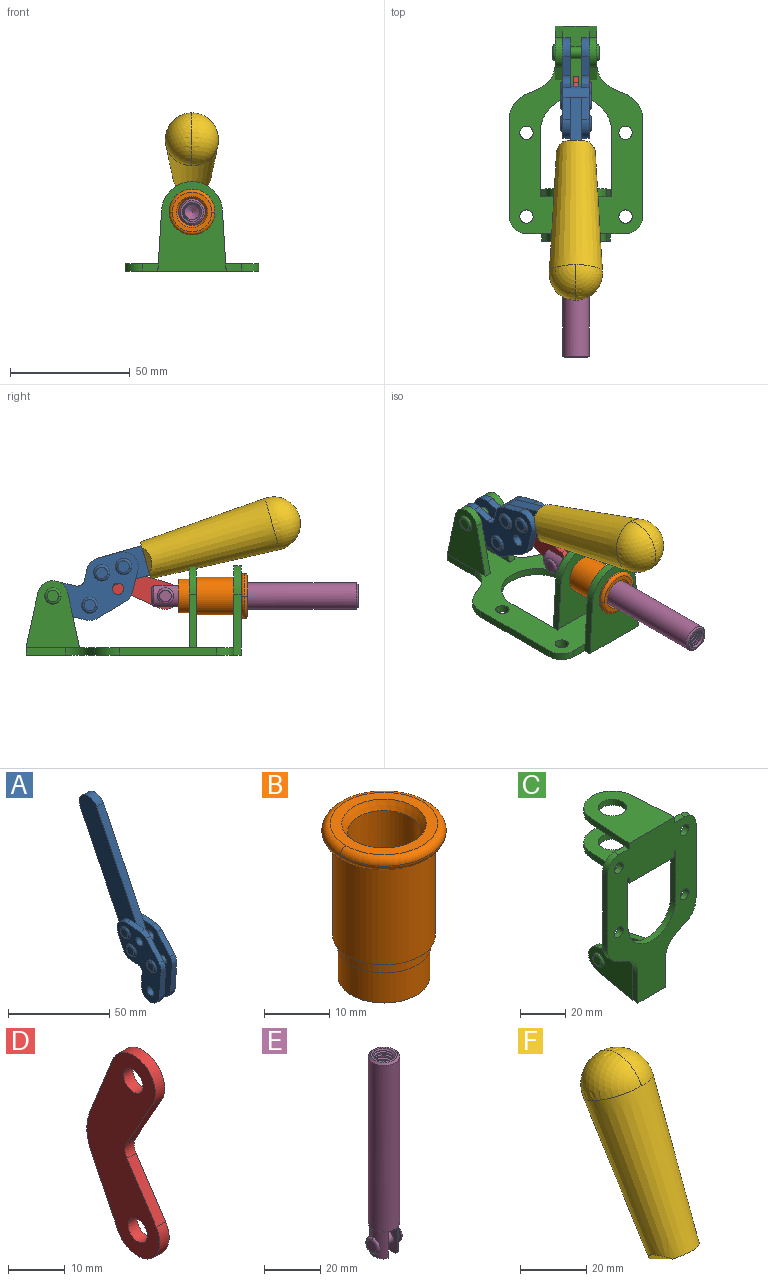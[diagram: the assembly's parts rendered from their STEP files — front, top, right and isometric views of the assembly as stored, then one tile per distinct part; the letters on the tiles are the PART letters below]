
ASSEMBLY  parts=6 mates=6
PART A: 59 faces, bbox 12.9x60.2x99.6 mm
  f0: torus R=2.39mm, axis (-1,0,0), area 14.9mm2, adj f20,f43,f51
  f1: torus R=2.39mm, axis (-1,0,0), area 14.9mm2, adj f19,f42,f51
  f2: torus R=2.39mm, axis (-1,0,0), area 14.9mm2, adj f18,f35,f51
  f3: torus R=2.39mm, axis (-1,0,0), area 14.9mm2, adj f14,f17,f23
  f4: torus R=2.39mm, axis (-1,0,0), area 14.9mm2, adj f13,f16,f23
  f5: torus R=2.39mm, axis (-1,0,0), area 14.9mm2, adj f12,f15,f23
  f6: cylinder r=2.39mm len=4.78mm, axis (1,0,0), area 46.5mm2, adj f48,f50,f51
  f7: cylinder r=2.39mm len=4.78mm, axis (1,0,0), area 46.5mm2, adj f50,f51
  f8: cylinder r=6.35mm len=12.68mm, axis (1,0,0), area 61.8mm2, adj f38,f39,f50,f51
  f9: cylinder r=2.39mm len=4.78mm, axis (-1,0,0), area 70.5mm2, adj f46,f50
  f10: cylinder r=2.39mm len=4.78mm, axis (-1,0,0), area 46.5mm2, adj f23,f45,f46
  f11: cylinder r=2.39mm len=4.78mm, axis (-1,0,0), area 46.5mm2, adj f23,f46
  f12: plane 4.78x4.78mm, normal (1,0,0), area 17.9mm2, adj f5,f15
  f13: plane 4.78x4.78mm, normal (1,0,0), area 17.9mm2, adj f4,f16
  f14: plane 4.78x4.78mm, normal (1,0,0), area 17.9mm2, adj f3,f17
  f15: torus R=2.39mm, axis (-1,0,0), area 14.9mm2, adj f5,f12,f23
  f16: torus R=2.39mm, axis (-1,0,0), area 14.9mm2, adj f4,f13,f23
  f17: torus R=2.39mm, axis (-1,0,0), area 14.9mm2, adj f3,f14,f23
  f18: plane 4.78x4.78mm, normal (-1,0,0), area 17.9mm2, adj f2,f35
  f19: plane 4.78x4.78mm, normal (-1,0,0), area 17.9mm2, adj f1,f42
  f20: plane 4.78x4.78mm, normal (-1,0,0), area 17.9mm2, adj f0,f43
  f21: plane 2.26x0.2mm, normal (1,0,0), area 0.2mm2, adj f31,f44
  f22: plane 2.26x0.2mm, normal (-1,0,0), area 0.2mm2, adj f41,f44
  f23: plane 39.37x30.77mm, normal (1,0,0), area 565.5mm2, adj f3,f4,f5,f10,f11,f15,f16,f17
  f24: cylinder r=6.1mm len=4.15mm, axis (-1,0,0), area 14.7mm2, adj f23,f25,f32,f46
  f25: plane 10.25x9.01mm, normal (0,-0.75,0.66), area 42.3mm2, adj f23,f24,f26,f46
  f26: cylinder r=6.35mm len=4.64mm, axis (-1,0,0), area 15.6mm2, adj f23,f25,f27,f46
  f27: plane 15.84x3.1mm, normal (0,-1,-0.07), area 49.2mm2, adj f23,f26,f28,f46
  f28: cylinder r=6.35mm len=12.68mm, axis (-1,0,0), area 61.8mm2, adj f23,f27,f29,f46
  f29: plane 8.11x3.1mm, normal (0,1,0.07), area 25.2mm2, adj f23,f28,f30,f46
  f30: cylinder r=3.05mm len=3.25mm, axis (-1,0,0), area 14.8mm2, adj f23,f29,f31,f46
  f31: plane 5.99x3.1mm, normal (0,0.07,-1), area 18.6mm2, adj f21,f23,f30,f44,f46
  f32: plane 9.5x3.1mm, normal (0,-0.07,1), area 29.5mm2, adj f23,f24,f33,f46,f47
  f33: cylinder r=6.1mm len=8.63mm, axis (-1,0,0), area 39.1mm2, adj f23,f32,f34,f47
  f34: plane 8.65x3.96mm, normal (0,0.91,-0.42), area 29.5mm2, adj f23,f33,f44,f47
  f35: torus R=2.39mm, axis (-1,0,0), area 14.9mm2, adj f2,f18,f51
  f36: plane 10.25x9.01mm, normal (0,-0.75,0.66), area 42.3mm2, adj f37,f49,f50,f51
  f37: cylinder r=6.35mm len=4.64mm, axis (1,0,0), area 15.6mm2, adj f36,f38,f50,f51
  f38: plane 15.84x3.1mm, normal (0,-1,-0.07), area 49.2mm2, adj f8,f37,f50,f51
  f39: plane 8.11x3.1mm, normal (0,1,0.07), area 25.2mm2, adj f8,f40,f50,f51
  f40: cylinder r=3.05mm len=3.25mm, axis (1,0,0), area 14.8mm2, adj f39,f41,f50,f51
  f41: plane 5.99x3.1mm, normal (0,0.07,-1), area 18.6mm2, adj f22,f40,f44,f50,f51
  f42: torus R=2.39mm, axis (-1,0,0), area 14.9mm2, adj f1,f19,f51
  f43: torus R=2.39mm, axis (-1,0,0), area 14.9mm2, adj f0,f20,f51
  f44: cylinder r=6.35mm len=12.12mm, axis (-1,0,0), area 128.9mm2, adj f21,f22,f23,f31,f34,f41,f46,f47
  f45: plane 2.65x1.35mm, normal (1,0,0), area 1mm2, adj f10,f55
  f46: plane 39.08x20.42mm, normal (-1,0,0), area 412.5mm2, adj f9,f10,f11,f24,f25,f26,f27,f28
  f47: plane 77.62x39.82mm, normal (1,0,0), area 850mm2, adj f32,f33,f34,f44,f53,f54,f55
  f48: plane 2.65x1.35mm, normal (-1,0,0), area 1mm2, adj f6,f55
  f49: cylinder r=6.1mm len=4.15mm, axis (1,0,0), area 14.7mm2, adj f36,f50,f51,f56
  f50: plane 39.08x20.42mm, normal (1,0,0), area 412.5mm2, adj f6,f7,f8,f9,f36,f37,f38,f39
  f51: plane 39.37x30.77mm, normal (-1,0,0), area 565.5mm2, adj f0,f1,f2,f6,f7,f8,f35,f36
  f52: plane 8.65x3.96mm, normal (0,0.91,-0.42), area 29.5mm2, adj f44,f51,f57,f58
  f53: plane 68.49x33.4mm, normal (0,0.9,-0.44), area 358.1mm2, adj f44,f47,f54,f58
  f54: cylinder r=6.35mm len=12.06mm, axis (1,0,0), area 93.7mm2, adj f47,f53,f55,f58
  f55: plane 68.49x33.4mm, normal (0,-0.9,0.44), area 358.1mm2, adj f44,f45,f46,f47,f48,f50,f54,f58
  f56: plane 9.5x3.1mm, normal (0,-0.07,1), area 29.5mm2, adj f49,f50,f51,f57,f58
  f57: cylinder r=6.1mm len=8.63mm, axis (1,0,0), area 39.1mm2, adj f51,f52,f56,f58
  f58: plane 77.62x39.82mm, normal (-1,0,0), area 850mm2, adj f44,f52,f53,f54,f55,f56,f57
PART B: 15 faces, bbox 20.6x20.6x28.7 mm
  f0: torus R=8.26mm, axis (0,0,1), area 56.8mm2, adj f1,f10,f12
  f1: torus R=8.26mm, axis (0,0,1), area 56.8mm2, adj f0,f6,f13
  f2: cylinder r=5.59mm len=25.91mm, axis (0,0,1), area 909.6mm2, adj f3,f4
  f3: cone r=6.86mm half-angle=45deg, axis (0,0,-1), area 70.2mm2, adj f2,f14
  f4: cone r=6.47mm half-angle=30deg, axis (0,0,1), area 66.7mm2, adj f2,f13
  f5: cylinder r=7.04mm len=14.07mm, axis (0,0,1), area 252.6mm2, adj f11,f14
  f6: torus R=8.26mm, axis (0,0,1), area 56.8mm2, adj f1,f12,f13
  f7: cylinder r=7.16mm len=14.33mm, axis (0,0,1), area 91.5mm2, adj f9,f11
  f8: cylinder r=7.86mm len=18.42mm, axis (0,0,1), area 909.6mm2, adj f9,f10
  f9: plane 15.72x15.72mm, normal (0,0,-1), area 33mm2, adj f7,f8
  f10: plane 16.51x16.51mm, normal (0,0,-1), area 19.9mm2, adj f0,f8,f12
  f11: plane 14.33x14.33mm, normal (0,0,-1), area 5.7mm2, adj f5,f7
  f12: torus R=8.26mm, axis (0,0,1), area 56.8mm2, adj f0,f6,f10
  f13: plane 16.51x16.51mm, normal (0,0,1), area 82.7mm2, adj f1,f4,f6
  f14: plane 14.07x14.07mm, normal (0,0,-1), area 7.8mm2, adj f3,f5
PART C: 55 faces, bbox 55.7x37.4x89.8 mm
  f0: torus R=2.41mm, axis (-1,0,0), area 15mm2, adj f11,f15,f25
  f1: torus R=2.41mm, axis (-1,0,0), area 15mm2, adj f10,f12,f22
  f2: cylinder r=2.78mm len=5.56mm, axis (0,-1,0), area 54.2mm2, adj f30,f54
  f3: cylinder r=14.99mm len=29.97mm, axis (0,-1,0), area 145.9mm2, adj f30,f49,f53,f54
  f4: cylinder r=2.78mm len=5.56mm, axis (0,-1,0), area 54.2mm2, adj f30,f54
  f5: cylinder r=2.78mm len=5.56mm, axis (0,-1,0), area 54.2mm2, adj f30,f54
  f6: cylinder r=2.78mm len=5.56mm, axis (0,-1,0), area 54.2mm2, adj f30,f54
  f7: cylinder r=6.35mm len=12.7mm, axis (0,0,1), area 123.6mm2, adj f27,f51
  f8: cylinder r=6.35mm len=12.7mm, axis (0,0,-1), area 124.7mm2, adj f21,f35
  f9: cylinder r=2.41mm len=11.18mm, axis (-1,0,0), area 169.4mm2, adj f16,f19
  f10: plane 4.83x4.83mm, normal (1,0,0), area 18.3mm2, adj f1,f12
  f11: plane 4.83x4.83mm, normal (-1,0,0), area 18.3mm2, adj f0,f15
  f12: torus R=2.41mm, axis (-1,0,0), area 15mm2, adj f1,f10,f22
  f13: cylinder r=6.35mm len=12.41mm, axis (1,0,0), area 53.4mm2, adj f18,f19,f22,f23
  f14: cylinder r=6.35mm len=12.41mm, axis (-1,0,0), area 53.4mm2, adj f16,f17,f24,f25
  f15: torus R=2.41mm, axis (-1,0,0), area 15mm2, adj f0,f11,f25
  f16: plane 27.86x22.35mm, normal (1,0,0), area 425.4mm2, adj f9,f14,f17,f24,f30
  f17: plane 22.86x4.97mm, normal (0,0.21,0.98), area 72.5mm2, adj f14,f16,f25,f30
  f18: plane 22.86x4.97mm, normal (0,0.21,0.98), area 72.5mm2, adj f13,f19,f22,f30
  f19: plane 27.86x22.35mm, normal (-1,0,0), area 425.4mm2, adj f9,f13,f18,f23,f30
  f20: cylinder r=12.7mm len=25.35mm, axis (0,0,-1), area 119.8mm2, adj f21,f34,f35,f36
  f21: plane 34.21x28.07mm, normal (0,0,-1), area 702.4mm2, adj f8,f20,f30,f34,f36
  f22: plane 27.96x22.45mm, normal (1,0,0), area 407.2mm2, adj f1,f12,f13,f18,f23,f30,f42,f43
  f23: plane 22.86x4.97mm, normal (0,0.21,-0.98), area 72.5mm2, adj f13,f19,f22,f44
  f24: plane 22.86x4.97mm, normal (0,0.21,-0.98), area 72.5mm2, adj f14,f16,f25,f44
  f25: plane 27.86x22.35mm, normal (-1,0,0), area 407.1mm2, adj f0,f14,f15,f17,f24,f30,f45,f46
  f26: plane 3.1x0.95mm, normal (0,0,-1), area 2.7mm2, adj f30,f49,f50,f54
  f27: plane 34.21x28.07mm, normal (0,0,1), area 702.4mm2, adj f7,f28,f30,f50,f52
  f28: cylinder r=12.7mm len=25.35mm, axis (0,0,1), area 118.8mm2, adj f27,f50,f51,f52
  f29: plane 3.1x0.95mm, normal (0,0,-1), area 2.7mm2, adj f30,f52,f53,f54
  f30: plane 86.54x55.63mm, normal (0,1,0), area 2362.9mm2, adj f2,f3,f4,f5,f6,f16,f17,f18
  f31: plane 40.56x3.1mm, normal (-1,0,0), area 125.7mm2, adj f30,f32,f48,f54
  f32: cylinder r=7.11mm len=7.11mm, axis (0,-1,0), area 34.6mm2, adj f30,f31,f33,f54
  f33: plane 6.67x3.1mm, normal (0,0,1), area 20.4mm2, adj f30,f32,f34,f54
  f34: plane 25.39x3.13mm, normal (-1,0.06,0), area 79.5mm2, adj f20,f21,f33,f35,f54
  f35: plane 37.31x28.45mm, normal (0,0,1), area 789.9mm2, adj f8,f20,f34,f36,f54
  f36: plane 25.39x3.13mm, normal (1,0.06,0), area 79.5mm2, adj f20,f21,f35,f37,f54
  f37: plane 6.67x3.1mm, normal (0,0,1), area 20.4mm2, adj f30,f36,f38,f54
  f38: cylinder r=7.11mm len=7.11mm, axis (0,-1,0), area 34.6mm2, adj f30,f37,f39,f54
  f39: plane 40.56x3.1mm, normal (1,0,0), area 125.7mm2, adj f30,f38,f40,f54
  f40: cylinder r=11.18mm len=10.16mm, axis (0,-1,0), area 39.5mm2, adj f30,f39,f41,f54
  f41: plane 6.09x3.1mm, normal (0.42,0,-0.91), area 20.8mm2, adj f30,f40,f42,f54
  f42: cylinder r=11.18mm len=9.41mm, axis (0,-1,0), area 37.2mm2, adj f22,f30,f41,f43,f54
  f43: plane 16.5x3.1mm, normal (1,0,0), area 51.1mm2, adj f22,f42,f44,f54
  f44: plane 17.37x3.1mm, normal (0,0,-1), area 53.8mm2, adj f23,f24,f30,f43,f45,f54
  f45: plane 16.5x3.1mm, normal (-1,0,0), area 51.1mm2, adj f25,f44,f46,f54
  f46: cylinder r=11.18mm len=9.41mm, axis (0,-1,0), area 37.2mm2, adj f25,f30,f45,f47,f54
  f47: plane 6.09x3.1mm, normal (-0.42,0,-0.91), area 20.8mm2, adj f30,f46,f48,f54
  f48: cylinder r=11.18mm len=10.16mm, axis (0,-1,0), area 39.5mm2, adj f30,f31,f47,f54
  f49: plane 26.54x3.1mm, normal (-1,0,0), area 82.3mm2, adj f3,f26,f30,f54
  f50: plane 25.39x3.1mm, normal (1,0.06,0), area 78.8mm2, adj f26,f27,f28,f51,f54
  f51: plane 37.31x28.45mm, normal (0,0,-1), area 789.9mm2, adj f7,f28,f50,f52,f54
  f52: plane 25.39x3.1mm, normal (-1,0.06,0), area 78.8mm2, adj f27,f28,f29,f51,f54
  f53: plane 26.54x3.1mm, normal (1,0,0), area 82.3mm2, adj f3,f29,f30,f54
  f54: plane 89.66x55.63mm, normal (0,-1,0), area 2678.5mm2, adj f2,f3,f4,f5,f6,f26,f29,f31
PART D: 12 faces, bbox 2.3x18.2x42.8 mm
  f0: cylinder r=2.4mm len=4.8mm, axis (1,0,0), area 34.9mm2, adj f4,f11
  f1: cylinder r=10.41mm len=8.47mm, axis (1,0,0), area 20.2mm2, adj f4,f9,f10,f11
  f2: cylinder r=3.05mm len=3.16mm, axis (1,0,0), area 7.7mm2, adj f4,f6,f7,f11
  f3: cylinder r=2.4mm len=4.8mm, axis (1,0,0), area 34.9mm2, adj f4,f11
  f4: plane 42.81x18.23mm, normal (-1,0,0), area 414.1mm2, adj f0,f1,f2,f3,f5,f6,f7,f8
  f5: cylinder r=5.54mm len=10.67mm, axis (1,0,0), area 41.8mm2, adj f4,f6,f10,f11
  f6: plane 11.66x6.53mm, normal (0,-0.87,-0.49), area 30.9mm2, adj f2,f4,f5,f11
  f7: plane 11.17x7.33mm, normal (0,-0.84,0.55), area 30.9mm2, adj f2,f4,f8,f11
  f8: cylinder r=5.54mm len=10.51mm, axis (1,0,0), area 41.8mm2, adj f4,f7,f9,f11
  f9: plane 13.67x6.67mm, normal (0,0.9,-0.44), area 35.1mm2, adj f1,f4,f8,f11
  f10: plane 14.1x5.7mm, normal (0,0.93,0.37), area 35.1mm2, adj f1,f4,f5,f11
  f11: plane 42.81x18.23mm, normal (1,0,0), area 414.1mm2, adj f0,f1,f2,f3,f5,f6,f7,f8
PART E: 48 faces, bbox 12.6x11.1x86.1 mm
  f0: torus R=2.41mm, axis (-1,0,0), area 15mm2, adj f30,f32,f34
  f1: torus R=2.41mm, axis (-1,0,0), area 15mm2, adj f29,f31,f33
  f2: cylinder r=5.54mm len=72.39mm, axis (0,0,1), area 2518.5mm2, adj f3,f4,f42,f43
  f3: cone r=5.54mm half-angle=45deg, axis (0,0,1), area 7.6mm2, adj f2,f5,f41
  f4: cone r=5.54mm half-angle=45deg, axis (0,0,-1), area 34.9mm2, adj f2,f39
  f5: cylinder r=5.08mm len=11.48mm, axis (0,0,1), area 108.3mm2, adj f3,f7,f8,f41
  f6: cylinder r=2.41mm len=4.83mm, axis (-1,0,0), area 71.2mm2, adj f40,f41
  f7: cylinder r=2.41mm len=4.83mm, axis (-1,0,0), area 7.6mm2, adj f5,f34
  f8: cone r=5.08mm half-angle=45deg, axis (0,0,1), area 10.6mm2, adj f5,f37,f41
  f9: cone r=3.98mm half-angle=45deg, axis (0,0,1), area 17.6mm2, adj f27,f39,f45,f46,f47
  f10: cylinder r=2.41mm len=4.83mm, axis (-1,0,0), area 7.6mm2, adj f33,f38
  f11: cylinder r=3.2mm len=6.4mm, axis (0,0,1), area 78.4mm2, adj f12,f28,f44,f45,f47
  f12: cylinder r=3.2mm len=6.4mm, axis (0,0,1), area 10.5mm2, adj f11,f13,f45,f47
  f13: cylinder r=3.2mm len=6.4mm, axis (0,0,1), area 10.5mm2, adj f12,f14,f45,f47
  f14: cylinder r=3.2mm len=6.4mm, axis (0,0,1), area 10.5mm2, adj f13,f15,f45,f47
  f15: cylinder r=3.2mm len=6.4mm, axis (0,0,1), area 10.5mm2, adj f14,f16,f45,f47
  f16: cylinder r=3.2mm len=6.4mm, axis (0,0,1), area 10.5mm2, adj f15,f17,f45,f47
  f17: cylinder r=3.2mm len=6.4mm, axis (0,0,1), area 10.5mm2, adj f16,f18,f45,f47
  f18: cylinder r=3.2mm len=6.4mm, axis (0,0,1), area 10.5mm2, adj f17,f19,f45,f47
  f19: cylinder r=3.2mm len=6.4mm, axis (0,0,1), area 10.5mm2, adj f18,f20,f45,f47
  f20: cylinder r=3.2mm len=6.4mm, axis (0,0,1), area 10.5mm2, adj f19,f21,f45,f47
  f21: cylinder r=3.2mm len=6.4mm, axis (0,0,1), area 10.5mm2, adj f20,f22,f45,f47
  f22: cylinder r=3.2mm len=6.4mm, axis (0,0,1), area 10.5mm2, adj f21,f23,f45,f47
  f23: cylinder r=3.2mm len=6.4mm, axis (0,0,1), area 10.5mm2, adj f22,f24,f45,f47
  f24: cylinder r=3.2mm len=6.4mm, axis (0,0,1), area 10.5mm2, adj f23,f25,f45,f47
  f25: cylinder r=3.2mm len=6.4mm, axis (0,0,1), area 10.5mm2, adj f24,f26,f45,f47
  f26: cylinder r=3.2mm len=6.4mm, axis (0,0,1), area 10.5mm2, adj f25,f27,f45,f47
  f27: cylinder r=3.2mm len=6.4mm, axis (0,0,1), area 7.4mm2, adj f9,f26,f45,f47
  f28: cone r=3.2mm half-angle=60deg, axis (0,0,1), area 37.2mm2, adj f11
  f29: plane 4.83x4.83mm, normal (-1,0,0), area 18.3mm2, adj f1,f31
  f30: plane 4.83x4.83mm, normal (1,0,0), area 18.3mm2, adj f0,f32
  f31: torus R=2.41mm, axis (-1,0,0), area 15mm2, adj f1,f29,f33
  f32: torus R=2.41mm, axis (-1,0,0), area 15mm2, adj f0,f30,f34
  f33: plane 6.83x6.83mm, normal (1,0,0), area 18.3mm2, adj f1,f10,f31
  f34: plane 6.83x6.83mm, normal (-1,0,0), area 18.3mm2, adj f0,f7,f32
  f35: cone r=5.08mm half-angle=45deg, axis (0,0,1), area 10.6mm2, adj f36,f38,f40
  f36: plane 7.25x1.97mm, normal (0,0,-1), area 10mm2, adj f35,f40
  f37: plane 7.25x1.97mm, normal (0,0,-1), area 10mm2, adj f8,f41
  f38: cylinder r=5.08mm len=11.48mm, axis (0,0,1), area 108.3mm2, adj f10,f35,f40,f42
  f39: plane 9.55x9.55mm, normal (0,0,1), area 22mm2, adj f4,f9
  f40: plane 12.76x10.09mm, normal (1,0,0), area 95.7mm2, adj f6,f35,f36,f38,f42,f43
  f41: plane 12.76x10.09mm, normal (-1,0,0), area 95.7mm2, adj f3,f5,f6,f8,f37,f43
  f42: cone r=5.54mm half-angle=45deg, axis (0,0,1), area 7.6mm2, adj f2,f38,f40
  f43: plane 11.07x4.7mm, normal (0,0,-1), area 50.4mm2, adj f2,f40,f41
  f44: plane 0.89x0.62mm, normal (-1,0,0), area 0.3mm2, adj f11,f45,f46,f47
  f45: bspline ~24.8x7.63mm, area 266.6mm2, adj f9,f11,f12,f13,f14,f15,f16,f17
  f46: bspline ~24.87x7.63mm, area 73.6mm2, adj f9,f44,f45,f47
  f47: bspline ~24.98x7.63mm, area 272.5mm2, adj f9,f11,f12,f13,f14,f15,f16,f17
PART F: 11 faces, bbox 22.3x42.6x64.5 mm
  f0: sphere r=11.13mm, area 411.4mm2, adj f1,f8
  f1: cone r=11.11mm half-angle=3.3deg, axis (0,0.44,0.9), area 3251.8mm2, adj f0,f7,f8,f9,f10
  f2: cylinder r=6.16mm len=11.7mm, axis (1,0,0), area 89.5mm2, adj f3,f4,f5,f6
  f3: plane 60.23x36.75mm, normal (-1,0,0), area 763.6mm2, adj f2,f4,f6,f10
  f4: plane 51.37x25.05mm, normal (0,0.9,-0.44), area 264.2mm2, adj f2,f3,f5,f10
  f5: plane 60.23x36.75mm, normal (1,0,0), area 763.6mm2, adj f2,f4,f6,f10
  f6: plane 51.37x25.05mm, normal (0,-0.9,0.44), area 264.2mm2, adj f2,f3,f5,f10
  f7: plane 9.95x5.95mm, normal (0.71,-0.31,-0.64), area 25.8mm2, adj f1,f10
  f8: sphere r=11.13mm, area 411.4mm2, adj f0,f1
  f9: plane 9.95x5.95mm, normal (-0.71,-0.31,-0.64), area 25.8mm2, adj f1,f10
  f10: plane 14.27x11.38mm, normal (0,-0.44,-0.9), area 106.7mm2, adj f1,f3,f4,f5,f6,f7,f9
PLACE A rot(axis=(1,0,0),100deg) t=(0,13.9,-5.2)mm
PLACE B rot(axis=(1,0,0),90deg) t=(0,9.14,0)mm
PLACE C rot(axis=(1,0,0),90deg) t=(0,9.14,0)mm fixed
PLACE D rot(axis=(1,0,0),85.1deg) t=(0,7.61,-1.24)mm
PLACE E rot(axis=(1,0,0),90deg) t=(0,9.79,0)mm
PLACE F rot(axis=(1,0,0),100deg) t=(-0.04,13.9,-5.2)mm
MATE revolute D.f3 <-> A.f4  axis (1,0,0) through (0,25.83,20.77)mm
MATE revolute D.f5 <-> E.f6  axis (1,0,0) through (0,-5.69,24.61)mm
MATE revolute A.f7 <-> C.f0  axis (-1,0,0) through (0,41.23,24.61)mm
MATE fastened B.f2 <-> C.f7  axis (0,1,0) through (0,-37.25,24.61)mm
MATE slider E.f2 <-> B.f2  axis (0,-1,0) through (0,-48.99,24.61)mm
MATE fastened F.f2 <-> A.f54  axis (1,0,0) through (-2.35,-52.38,55.25)mm
